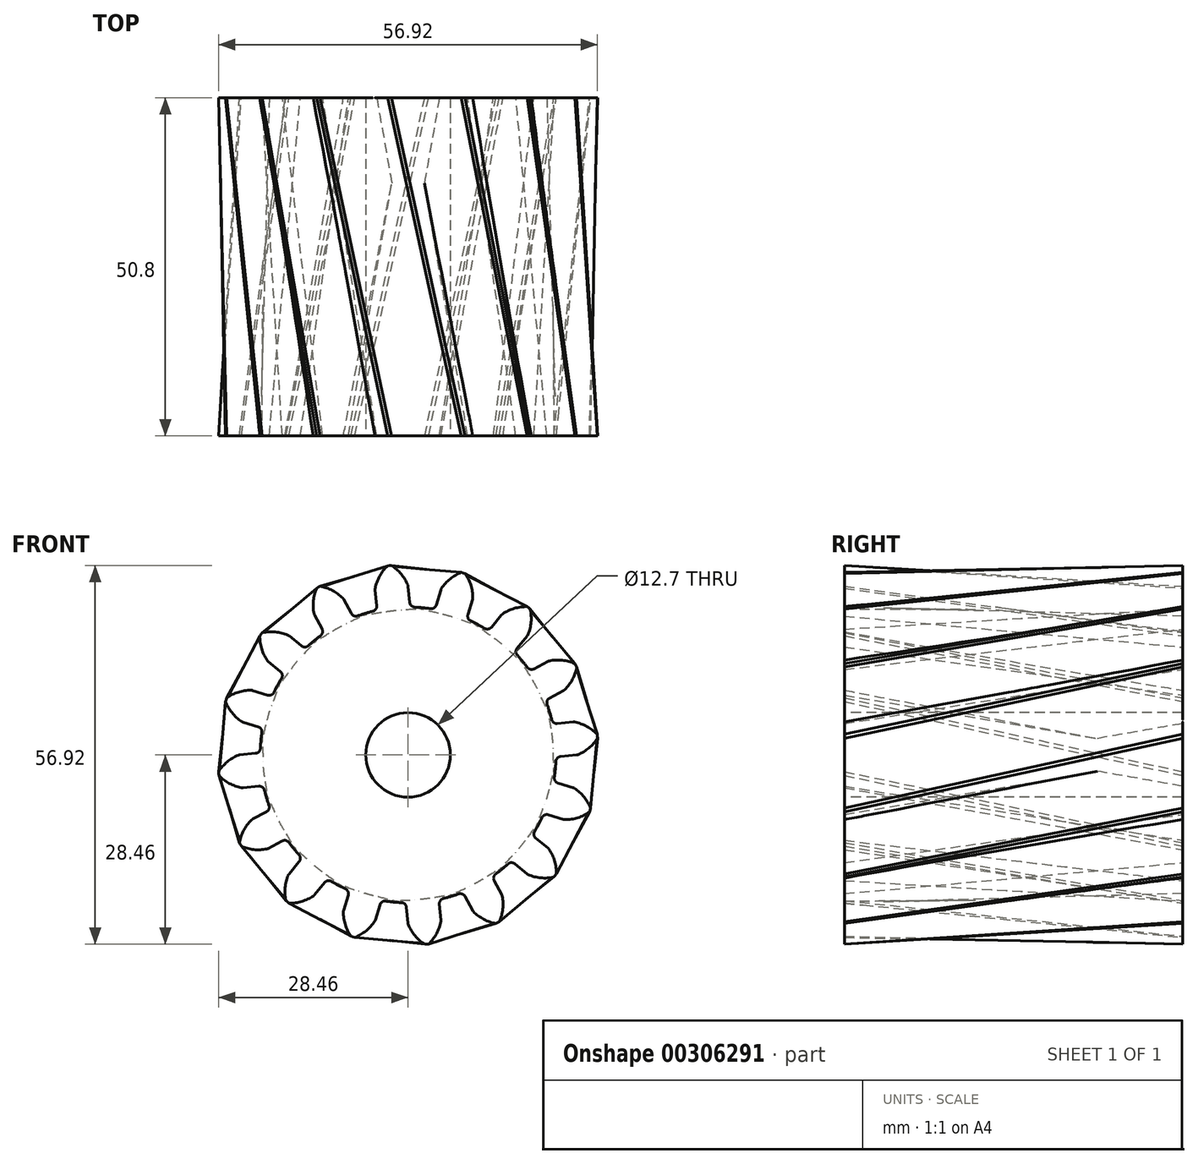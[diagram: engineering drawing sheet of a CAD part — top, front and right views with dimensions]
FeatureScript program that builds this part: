
annotation { "Feature Type Name" : "Feature", "Feature Type Description" : "" }
export const myFeature = defineFeature(function(context is Context, id is Id, definition is map)
    precondition{}
    {
        {
            var Q0;
            Q0=qCreatedBy(makeId("Front.planeOp"),FACE);
            var sketch = newSketch(context, id + "F0", { "sketchPlane" : qUnion([Q0])});
            skArc(sketch, "E0", {"start": v(-5.3, 21.58) * mm, "mid": v(-6.45, 21.27) * mm, "end": v(-7.58, 20.9) * mm});
            skArc(sketch, "E1.trimOffspring", {"start": v(-0.04, 25.51) * mm, "mid": v(-1.05, 27.18) * mm, "end": v(-2.5, 28.46) * mm});
            skLineSegment(sketch, "E2", {"start": v(-2.5, 28.46) * mm, "end": v(-2.8, 28.44) * mm});
            skLineSegment(sketch, "E3", {"start": v(0.01, 25.29) * mm, "end": v(0.25, 22.91) * mm});
            skLineSegment(sketch, "E4.MirrorCS", {"start": v(-3.1, 28.4) * mm, "end": v(-2.8, 28.44) * mm});
            skArc(sketch, "E5.MirrorCS", {"start": v(-4.93, 25.03) * mm, "mid": v(-4.28, 26.86) * mm, "end": v(-3.1, 28.4) * mm});
            skLineSegment(sketch, "E6.MirrorCS", {"start": v(-4.94, 24.8) * mm, "end": v(-4.71, 22.42) * mm});
            skPoint(sketch, "E7.orphan", {"position": v(-4.37, 19) * mm});
            skPoint(sketch, "E8.orphan", {"position": v(0.58, 19.48) * mm});
            skPoint(sketch, "E9.visualSharp", {"position": v(-4.96, 24.91) * mm});
            skArc(sketch, "E9.filletArc", {"start": v(-4.93, 25.03) * mm, "mid": v(-4.95, 24.92) * mm, "end": v(-4.94, 24.8) * mm});
            skPoint(sketch, "E10.visualSharp", {"position": v(0, 25.4) * mm});
            skArc(sketch, "E10.filletArc", {"start": v(0.01, 25.29) * mm, "mid": v(0, 25.4) * mm, "end": v(-0.04, 25.51) * mm});
            skPoint(sketch, "E11.visualSharp", {"position": v(0.31, 22.22) * mm});
            skArc(sketch, "E11.filletArc", {"start": v(0.25, 22.91) * mm, "mid": v(0.49, 22.42) * mm, "end": v(1, 22.2) * mm});
            skPoint(sketch, "E12.visualSharp", {"position": v(-4.64, 21.73) * mm});
            skArc(sketch, "E12.filletArc", {"start": v(-5.3, 21.58) * mm, "mid": v(-4.85, 21.9) * mm, "end": v(-4.71, 22.42) * mm});
            skArc(sketch, "E13.1.0", {"start": v(-14.14, 21.24) * mm, "mid": v(-14.23, 23.18) * mm, "end": v(-13.73, 25.06) * mm});
            skArc(sketch, "E13.1.1", {"start": v(-14.14, 21.24) * mm, "mid": v(-14.1, 21.13) * mm, "end": v(-14.06, 21.02) * mm});
            skLineSegment(sketch, "E13.1.2", {"start": v(-14.06, 21.02) * mm, "end": v(-12.93, 18.91) * mm});
            skArc(sketch, "E13.1.3", {"start": v(-9.67, 23.37) * mm, "mid": v(-9.73, 23.47) * mm, "end": v(-9.8, 23.55) * mm});
            skArc(sketch, "E13.1.4", {"start": v(-9.8, 23.55) * mm, "mid": v(-11.37, 24.7) * mm, "end": v(-13.21, 25.34) * mm});
            skLineSegment(sketch, "E13.1.5", {"start": v(-9.67, 23.37) * mm, "end": v(-8.54, 21.26) * mm});
            skLineSegment(sketch, "E13.1.6", {"start": v(-13.21, 25.34) * mm, "end": v(-13.47, 25.2) * mm});
            skLineSegment(sketch, "E13.1.7", {"start": v(-13.73, 25.06) * mm, "end": v(-13.47, 25.2) * mm});
            skArc(sketch, "E13.1.8", {"start": v(-13.16, 17.9) * mm, "mid": v(-12.86, 18.37) * mm, "end": v(-12.93, 18.91) * mm});
            skArc(sketch, "E13.1.9", {"start": v(-8.54, 21.26) * mm, "mid": v(-8.13, 20.9) * mm, "end": v(-7.58, 20.9) * mm});
            skArc(sketch, "E13.2.0", {"start": v(-21.19, 14.2) * mm, "mid": v(-22.02, 15.97) * mm, "end": v(-22.27, 17.9) * mm});
            skArc(sketch, "E13.2.1", {"start": v(-21.19, 14.2) * mm, "mid": v(-21.12, 14.12) * mm, "end": v(-21.03, 14.04) * mm});
            skLineSegment(sketch, "E13.2.2", {"start": v(-21.03, 14.04) * mm, "end": v(-19.19, 12.53) * mm});
            skArc(sketch, "E13.2.3", {"start": v(-17.87, 17.9) * mm, "mid": v(-17.97, 17.96) * mm, "end": v(-18.07, 18) * mm});
            skArc(sketch, "E13.2.4", {"start": v(-18.07, 18) * mm, "mid": v(-19.96, 18.48) * mm, "end": v(-21.9, 18.35) * mm});
            skLineSegment(sketch, "E13.2.5", {"start": v(-17.87, 17.9) * mm, "end": v(-16.03, 16.37) * mm});
            skLineSegment(sketch, "E13.2.6", {"start": v(-21.9, 18.35) * mm, "end": v(-22.09, 18.13) * mm});
            skLineSegment(sketch, "E13.2.7", {"start": v(-22.27, 17.9) * mm, "end": v(-22.09, 18.13) * mm});
            skArc(sketch, "E13.2.8", {"start": v(-19.01, 11.5) * mm, "mid": v(-18.91, 12.05) * mm, "end": v(-19.19, 12.53) * mm});
            skArc(sketch, "E13.2.9", {"start": v(-16.03, 16.37) * mm, "mid": v(-15.5, 16.2) * mm, "end": v(-15, 16.4) * mm});
            skArc(sketch, "E14.2.3.0", {"start": v(-25.01, 5.02) * mm, "mid": v(-26.45, 6.33) * mm, "end": v(-27.43, 8.01) * mm});
            skArc(sketch, "E14.4.3.0", {"start": v(-25.01, 5.02) * mm, "mid": v(-24.91, 4.96) * mm, "end": v(-24.8, 4.92) * mm});
            skLineSegment(sketch, "E14.8.3.0", {"start": v(-24.8, 4.92) * mm, "end": v(-22.52, 4.23) * mm});
            skArc(sketch, "E14.11.3.0", {"start": v(-23.36, 9.69) * mm, "mid": v(-23.47, 9.71) * mm, "end": v(-23.58, 9.72) * mm});
            skArc(sketch, "E14.15.3.0", {"start": v(-23.58, 9.72) * mm, "mid": v(-25.51, 9.43) * mm, "end": v(-27.26, 8.58) * mm});
            skLineSegment(sketch, "E14.19.3.0", {"start": v(-23.36, 9.69) * mm, "end": v(-21.07, 9) * mm});
            skLineSegment(sketch, "E14.22.3.0", {"start": v(-27.26, 8.58) * mm, "end": v(-27.35, 8.3) * mm});
            skLineSegment(sketch, "E14.25.3.0", {"start": v(-27.43, 8.01) * mm, "end": v(-27.35, 8.3) * mm});
            skArc(sketch, "E14.28.3.0", {"start": v(-21.97, 3.36) * mm, "mid": v(-22.08, 3.9) * mm, "end": v(-22.52, 4.23) * mm});
            skArc(sketch, "E14.32.3.0", {"start": v(-21.07, 9) * mm, "mid": v(-20.53, 9.03) * mm, "end": v(-20.13, 9.41) * mm});
            skArc(sketch, "E14.2.4.0", {"start": v(-25.03, -4.93) * mm, "mid": v(-26.86, -4.28) * mm, "end": v(-28.4, -3.1) * mm});
            skArc(sketch, "E14.4.4.0", {"start": v(-25.03, -4.93) * mm, "mid": v(-24.92, -4.95) * mm, "end": v(-24.8, -4.94) * mm});
            skLineSegment(sketch, "E14.8.4.0", {"start": v(-24.8, -4.94) * mm, "end": v(-22.42, -4.71) * mm});
            skArc(sketch, "E14.11.4.0", {"start": v(-25.29, 0.01) * mm, "mid": v(-25.4, 0) * mm, "end": v(-25.51, -0.04) * mm});
            skArc(sketch, "E14.15.4.0", {"start": v(-25.51, -0.04) * mm, "mid": v(-27.18, -1.05) * mm, "end": v(-28.46, -2.5) * mm});
            skLineSegment(sketch, "E14.19.4.0", {"start": v(-25.29, 0.01) * mm, "end": v(-22.91, 0.25) * mm});
            skLineSegment(sketch, "E14.22.4.0", {"start": v(-28.46, -2.5) * mm, "end": v(-28.44, -2.8) * mm});
            skLineSegment(sketch, "E14.25.4.0", {"start": v(-28.4, -3.1) * mm, "end": v(-28.44, -2.8) * mm});
            skArc(sketch, "E14.28.4.0", {"start": v(-21.58, -5.3) * mm, "mid": v(-21.9, -4.85) * mm, "end": v(-22.42, -4.71) * mm});
            skArc(sketch, "E14.32.4.0", {"start": v(-22.91, 0.25) * mm, "mid": v(-22.42, 0.49) * mm, "end": v(-22.2, 1) * mm});
            skArc(sketch, "E14.2.5.0", {"start": v(-21.24, -14.14) * mm, "mid": v(-23.18, -14.23) * mm, "end": v(-25.06, -13.73) * mm});
            skArc(sketch, "E14.4.5.0", {"start": v(-21.24, -14.14) * mm, "mid": v(-21.13, -14.1) * mm, "end": v(-21.02, -14.06) * mm});
            skLineSegment(sketch, "E14.8.5.0", {"start": v(-21.02, -14.06) * mm, "end": v(-18.91, -12.93) * mm});
            skArc(sketch, "E14.11.5.0", {"start": v(-23.37, -9.67) * mm, "mid": v(-23.47, -9.73) * mm, "end": v(-23.55, -9.8) * mm});
            skArc(sketch, "E14.15.5.0", {"start": v(-23.55, -9.8) * mm, "mid": v(-24.7, -11.37) * mm, "end": v(-25.34, -13.21) * mm});
            skLineSegment(sketch, "E14.19.5.0", {"start": v(-23.37, -9.67) * mm, "end": v(-21.26, -8.54) * mm});
            skLineSegment(sketch, "E14.22.5.0", {"start": v(-25.34, -13.21) * mm, "end": v(-25.2, -13.47) * mm});
            skLineSegment(sketch, "E14.25.5.0", {"start": v(-25.06, -13.73) * mm, "end": v(-25.2, -13.47) * mm});
            skArc(sketch, "E14.28.5.0", {"start": v(-17.9, -13.16) * mm, "mid": v(-18.37, -12.86) * mm, "end": v(-18.91, -12.93) * mm});
            skArc(sketch, "E14.32.5.0", {"start": v(-21.26, -8.54) * mm, "mid": v(-20.9, -8.13) * mm, "end": v(-20.9, -7.58) * mm});
            skArc(sketch, "E14.2.6.0", {"start": v(-14.2, -21.19) * mm, "mid": v(-15.97, -22.02) * mm, "end": v(-17.9, -22.27) * mm});
            skArc(sketch, "E14.4.6.0", {"start": v(-14.2, -21.19) * mm, "mid": v(-14.12, -21.12) * mm, "end": v(-14.04, -21.03) * mm});
            skLineSegment(sketch, "E14.8.6.0", {"start": v(-14.04, -21.03) * mm, "end": v(-12.53, -19.19) * mm});
            skArc(sketch, "E14.11.6.0", {"start": v(-17.9, -17.87) * mm, "mid": v(-17.96, -17.97) * mm, "end": v(-18, -18.07) * mm});
            skArc(sketch, "E14.15.6.0", {"start": v(-18, -18.07) * mm, "mid": v(-18.48, -19.96) * mm, "end": v(-18.35, -21.9) * mm});
            skLineSegment(sketch, "E14.19.6.0", {"start": v(-17.9, -17.87) * mm, "end": v(-16.37, -16.03) * mm});
            skLineSegment(sketch, "E14.22.6.0", {"start": v(-18.35, -21.9) * mm, "end": v(-18.13, -22.09) * mm});
            skLineSegment(sketch, "E14.25.6.0", {"start": v(-17.9, -22.27) * mm, "end": v(-18.13, -22.09) * mm});
            skArc(sketch, "E14.28.6.0", {"start": v(-11.5, -19.01) * mm, "mid": v(-12.05, -18.91) * mm, "end": v(-12.53, -19.19) * mm});
            skArc(sketch, "E14.32.6.0", {"start": v(-16.37, -16.03) * mm, "mid": v(-16.2, -15.5) * mm, "end": v(-16.4, -15) * mm});
            skArc(sketch, "E14.2.7.0", {"start": v(-5.02, -25.01) * mm, "mid": v(-6.33, -26.45) * mm, "end": v(-8.01, -27.43) * mm});
            skArc(sketch, "E14.4.7.0", {"start": v(-5.02, -25.01) * mm, "mid": v(-4.96, -24.91) * mm, "end": v(-4.92, -24.8) * mm});
            skLineSegment(sketch, "E14.8.7.0", {"start": v(-4.92, -24.8) * mm, "end": v(-4.23, -22.52) * mm});
            skArc(sketch, "E14.11.7.0", {"start": v(-9.69, -23.36) * mm, "mid": v(-9.71, -23.47) * mm, "end": v(-9.72, -23.58) * mm});
            skArc(sketch, "E14.15.7.0", {"start": v(-9.72, -23.58) * mm, "mid": v(-9.43, -25.51) * mm, "end": v(-8.58, -27.26) * mm});
            skLineSegment(sketch, "E14.19.7.0", {"start": v(-9.69, -23.36) * mm, "end": v(-9, -21.07) * mm});
            skLineSegment(sketch, "E14.22.7.0", {"start": v(-8.58, -27.26) * mm, "end": v(-8.3, -27.35) * mm});
            skLineSegment(sketch, "E14.25.7.0", {"start": v(-8.01, -27.43) * mm, "end": v(-8.3, -27.35) * mm});
            skArc(sketch, "E14.28.7.0", {"start": v(-3.36, -21.97) * mm, "mid": v(-3.9, -22.08) * mm, "end": v(-4.23, -22.52) * mm});
            skArc(sketch, "E14.32.7.0", {"start": v(-9, -21.07) * mm, "mid": v(-9.03, -20.53) * mm, "end": v(-9.41, -20.13) * mm});
            skArc(sketch, "E14.2.8.0", {"start": v(4.93, -25.03) * mm, "mid": v(4.28, -26.86) * mm, "end": v(3.1, -28.4) * mm});
            skArc(sketch, "E14.4.8.0", {"start": v(4.93, -25.03) * mm, "mid": v(4.95, -24.92) * mm, "end": v(4.94, -24.8) * mm});
            skLineSegment(sketch, "E14.8.8.0", {"start": v(4.94, -24.8) * mm, "end": v(4.71, -22.42) * mm});
            skArc(sketch, "E14.11.8.0", {"start": v(-0.01, -25.29) * mm, "mid": v(0, -25.4) * mm, "end": v(0.04, -25.51) * mm});
            skArc(sketch, "E14.15.8.0", {"start": v(0.04, -25.51) * mm, "mid": v(1.05, -27.18) * mm, "end": v(2.5, -28.46) * mm});
            skLineSegment(sketch, "E14.19.8.0", {"start": v(-0.01, -25.29) * mm, "end": v(-0.25, -22.91) * mm});
            skLineSegment(sketch, "E14.22.8.0", {"start": v(2.5, -28.46) * mm, "end": v(2.8, -28.44) * mm});
            skLineSegment(sketch, "E14.25.8.0", {"start": v(3.1, -28.4) * mm, "end": v(2.8, -28.44) * mm});
            skArc(sketch, "E14.28.8.0", {"start": v(5.3, -21.58) * mm, "mid": v(4.85, -21.9) * mm, "end": v(4.71, -22.42) * mm});
            skArc(sketch, "E14.32.8.0", {"start": v(-0.25, -22.91) * mm, "mid": v(-0.49, -22.42) * mm, "end": v(-1, -22.2) * mm});
            skArc(sketch, "E14.2.9.0", {"start": v(14.14, -21.24) * mm, "mid": v(14.23, -23.18) * mm, "end": v(13.73, -25.06) * mm});
            skArc(sketch, "E14.4.9.0", {"start": v(14.14, -21.24) * mm, "mid": v(14.1, -21.13) * mm, "end": v(14.06, -21.02) * mm});
            skLineSegment(sketch, "E14.8.9.0", {"start": v(14.06, -21.02) * mm, "end": v(12.93, -18.91) * mm});
            skArc(sketch, "E14.11.9.0", {"start": v(9.67, -23.37) * mm, "mid": v(9.73, -23.47) * mm, "end": v(9.8, -23.55) * mm});
            skArc(sketch, "E14.15.9.0", {"start": v(9.8, -23.55) * mm, "mid": v(11.37, -24.7) * mm, "end": v(13.21, -25.34) * mm});
            skLineSegment(sketch, "E14.19.9.0", {"start": v(9.67, -23.37) * mm, "end": v(8.54, -21.26) * mm});
            skLineSegment(sketch, "E14.22.9.0", {"start": v(13.21, -25.34) * mm, "end": v(13.47, -25.2) * mm});
            skLineSegment(sketch, "E14.25.9.0", {"start": v(13.73, -25.06) * mm, "end": v(13.47, -25.2) * mm});
            skArc(sketch, "E14.28.9.0", {"start": v(13.16, -17.9) * mm, "mid": v(12.86, -18.37) * mm, "end": v(12.93, -18.91) * mm});
            skArc(sketch, "E14.32.9.0", {"start": v(8.54, -21.26) * mm, "mid": v(8.13, -20.9) * mm, "end": v(7.58, -20.9) * mm});
            skArc(sketch, "E14.2.10.0", {"start": v(21.19, -14.2) * mm, "mid": v(22.02, -15.97) * mm, "end": v(22.27, -17.9) * mm});
            skArc(sketch, "E14.4.10.0", {"start": v(21.19, -14.2) * mm, "mid": v(21.12, -14.12) * mm, "end": v(21.03, -14.04) * mm});
            skLineSegment(sketch, "E14.8.10.0", {"start": v(21.03, -14.04) * mm, "end": v(19.19, -12.53) * mm});
            skArc(sketch, "E14.11.10.0", {"start": v(17.87, -17.9) * mm, "mid": v(17.97, -17.96) * mm, "end": v(18.07, -18) * mm});
            skArc(sketch, "E14.15.10.0", {"start": v(18.07, -18) * mm, "mid": v(19.96, -18.48) * mm, "end": v(21.9, -18.35) * mm});
            skLineSegment(sketch, "E14.19.10.0", {"start": v(17.87, -17.9) * mm, "end": v(16.03, -16.37) * mm});
            skLineSegment(sketch, "E14.22.10.0", {"start": v(21.9, -18.35) * mm, "end": v(22.09, -18.13) * mm});
            skLineSegment(sketch, "E14.25.10.0", {"start": v(22.27, -17.9) * mm, "end": v(22.09, -18.13) * mm});
            skArc(sketch, "E14.28.10.0", {"start": v(19.01, -11.5) * mm, "mid": v(18.91, -12.05) * mm, "end": v(19.19, -12.53) * mm});
            skArc(sketch, "E14.32.10.0", {"start": v(16.03, -16.37) * mm, "mid": v(15.5, -16.2) * mm, "end": v(15, -16.4) * mm});
            skArc(sketch, "E14.2.11.0", {"start": v(25.01, -5.02) * mm, "mid": v(26.45, -6.33) * mm, "end": v(27.43, -8.01) * mm});
            skArc(sketch, "E14.4.11.0", {"start": v(25.01, -5.02) * mm, "mid": v(24.91, -4.96) * mm, "end": v(24.8, -4.92) * mm});
            skLineSegment(sketch, "E14.8.11.0", {"start": v(24.8, -4.92) * mm, "end": v(22.52, -4.23) * mm});
            skArc(sketch, "E14.11.11.0", {"start": v(23.36, -9.69) * mm, "mid": v(23.47, -9.71) * mm, "end": v(23.58, -9.72) * mm});
            skArc(sketch, "E14.15.11.0", {"start": v(23.58, -9.72) * mm, "mid": v(25.51, -9.43) * mm, "end": v(27.26, -8.58) * mm});
            skLineSegment(sketch, "E14.19.11.0", {"start": v(23.36, -9.69) * mm, "end": v(21.07, -9) * mm});
            skLineSegment(sketch, "E14.22.11.0", {"start": v(27.26, -8.58) * mm, "end": v(27.35, -8.3) * mm});
            skLineSegment(sketch, "E14.25.11.0", {"start": v(27.43, -8.01) * mm, "end": v(27.35, -8.3) * mm});
            skArc(sketch, "E14.28.11.0", {"start": v(21.97, -3.36) * mm, "mid": v(22.08, -3.9) * mm, "end": v(22.52, -4.23) * mm});
            skArc(sketch, "E14.32.11.0", {"start": v(21.07, -9) * mm, "mid": v(20.53, -9.03) * mm, "end": v(20.13, -9.41) * mm});
            skArc(sketch, "E14.2.12.0", {"start": v(25.03, 4.93) * mm, "mid": v(26.86, 4.28) * mm, "end": v(28.4, 3.1) * mm});
            skArc(sketch, "E14.4.12.0", {"start": v(25.03, 4.93) * mm, "mid": v(24.92, 4.95) * mm, "end": v(24.8, 4.94) * mm});
            skLineSegment(sketch, "E14.8.12.0", {"start": v(24.8, 4.94) * mm, "end": v(22.42, 4.71) * mm});
            skArc(sketch, "E14.11.12.0", {"start": v(25.29, -0.01) * mm, "mid": v(25.4, 0) * mm, "end": v(25.51, 0.04) * mm});
            skArc(sketch, "E14.15.12.0", {"start": v(25.51, 0.04) * mm, "mid": v(27.18, 1.05) * mm, "end": v(28.46, 2.5) * mm});
            skLineSegment(sketch, "E14.19.12.0", {"start": v(25.29, -0.01) * mm, "end": v(22.91, -0.25) * mm});
            skLineSegment(sketch, "E14.22.12.0", {"start": v(28.46, 2.5) * mm, "end": v(28.44, 2.8) * mm});
            skLineSegment(sketch, "E14.25.12.0", {"start": v(28.4, 3.1) * mm, "end": v(28.44, 2.8) * mm});
            skArc(sketch, "E14.28.12.0", {"start": v(21.58, 5.3) * mm, "mid": v(21.9, 4.85) * mm, "end": v(22.42, 4.71) * mm});
            skArc(sketch, "E14.32.12.0", {"start": v(22.91, -0.25) * mm, "mid": v(22.42, -0.49) * mm, "end": v(22.2, -1) * mm});
            skArc(sketch, "E14.2.13.0", {"start": v(21.24, 14.14) * mm, "mid": v(23.18, 14.23) * mm, "end": v(25.06, 13.73) * mm});
            skArc(sketch, "E14.4.13.0", {"start": v(21.24, 14.14) * mm, "mid": v(21.13, 14.1) * mm, "end": v(21.02, 14.06) * mm});
            skLineSegment(sketch, "E14.8.13.0", {"start": v(21.02, 14.06) * mm, "end": v(18.91, 12.93) * mm});
            skArc(sketch, "E14.11.13.0", {"start": v(23.37, 9.67) * mm, "mid": v(23.47, 9.73) * mm, "end": v(23.55, 9.8) * mm});
            skArc(sketch, "E14.15.13.0", {"start": v(23.55, 9.8) * mm, "mid": v(24.7, 11.37) * mm, "end": v(25.34, 13.21) * mm});
            skLineSegment(sketch, "E14.19.13.0", {"start": v(23.37, 9.67) * mm, "end": v(21.26, 8.54) * mm});
            skLineSegment(sketch, "E14.22.13.0", {"start": v(25.34, 13.21) * mm, "end": v(25.2, 13.47) * mm});
            skLineSegment(sketch, "E14.25.13.0", {"start": v(25.06, 13.73) * mm, "end": v(25.2, 13.47) * mm});
            skArc(sketch, "E14.28.13.0", {"start": v(17.9, 13.16) * mm, "mid": v(18.37, 12.86) * mm, "end": v(18.91, 12.93) * mm});
            skArc(sketch, "E14.32.13.0", {"start": v(21.26, 8.54) * mm, "mid": v(20.9, 8.13) * mm, "end": v(20.9, 7.58) * mm});
            skArc(sketch, "E14.2.14.0", {"start": v(14.2, 21.19) * mm, "mid": v(15.97, 22.02) * mm, "end": v(17.9, 22.27) * mm});
            skArc(sketch, "E14.4.14.0", {"start": v(14.2, 21.19) * mm, "mid": v(14.12, 21.12) * mm, "end": v(14.04, 21.03) * mm});
            skLineSegment(sketch, "E14.8.14.0", {"start": v(14.04, 21.03) * mm, "end": v(12.53, 19.19) * mm});
            skArc(sketch, "E14.11.14.0", {"start": v(17.9, 17.87) * mm, "mid": v(17.96, 17.97) * mm, "end": v(18, 18.07) * mm});
            skArc(sketch, "E14.15.14.0", {"start": v(18, 18.07) * mm, "mid": v(18.48, 19.96) * mm, "end": v(18.35, 21.9) * mm});
            skLineSegment(sketch, "E14.19.14.0", {"start": v(17.9, 17.87) * mm, "end": v(16.37, 16.03) * mm});
            skLineSegment(sketch, "E14.22.14.0", {"start": v(18.35, 21.9) * mm, "end": v(18.13, 22.09) * mm});
            skLineSegment(sketch, "E14.25.14.0", {"start": v(17.9, 22.27) * mm, "end": v(18.13, 22.09) * mm});
            skArc(sketch, "E14.28.14.0", {"start": v(11.5, 19.01) * mm, "mid": v(12.05, 18.91) * mm, "end": v(12.53, 19.19) * mm});
            skArc(sketch, "E14.32.14.0", {"start": v(16.37, 16.03) * mm, "mid": v(16.2, 15.5) * mm, "end": v(16.4, 15) * mm});
            skArc(sketch, "E14.2.15.0", {"start": v(5.02, 25.01) * mm, "mid": v(6.33, 26.45) * mm, "end": v(8.01, 27.43) * mm});
            skArc(sketch, "E14.4.15.0", {"start": v(5.02, 25.01) * mm, "mid": v(4.96, 24.91) * mm, "end": v(4.92, 24.8) * mm});
            skLineSegment(sketch, "E14.8.15.0", {"start": v(4.92, 24.8) * mm, "end": v(4.23, 22.52) * mm});
            skArc(sketch, "E14.11.15.0", {"start": v(9.69, 23.36) * mm, "mid": v(9.71, 23.47) * mm, "end": v(9.72, 23.58) * mm});
            skArc(sketch, "E14.15.15.0", {"start": v(9.72, 23.58) * mm, "mid": v(9.43, 25.51) * mm, "end": v(8.58, 27.26) * mm});
            skLineSegment(sketch, "E14.19.15.0", {"start": v(9.69, 23.36) * mm, "end": v(9, 21.07) * mm});
            skLineSegment(sketch, "E14.22.15.0", {"start": v(8.58, 27.26) * mm, "end": v(8.3, 27.35) * mm});
            skLineSegment(sketch, "E14.25.15.0", {"start": v(8.01, 27.43) * mm, "end": v(8.3, 27.35) * mm});
            skArc(sketch, "E14.28.15.0", {"start": v(3.36, 21.97) * mm, "mid": v(3.9, 22.08) * mm, "end": v(4.23, 22.52) * mm});
            skArc(sketch, "E14.32.15.0", {"start": v(9, 21.07) * mm, "mid": v(9.03, 20.53) * mm, "end": v(9.41, 20.13) * mm});
            skArc(sketch, "E15.trimOffspring", {"start": v(-13.16, 17.9) * mm, "mid": v(-14.1, 17.18) * mm, "end": v(-15, 16.4) * mm});
            skArc(sketch, "E16.trimOffspring", {"start": v(-19.01, 11.5) * mm, "mid": v(-19.6, 10.48) * mm, "end": v(-20.13, 9.41) * mm});
            skArc(sketch, "E17.trimOffspring", {"start": v(-21.97, 3.36) * mm, "mid": v(-22.12, 2.18) * mm, "end": v(-22.2, 1) * mm});
            skArc(sketch, "E18.trimOffspring", {"start": v(-21.58, -5.3) * mm, "mid": v(-21.27, -6.45) * mm, "end": v(-20.9, -7.58) * mm});
            skArc(sketch, "E19.trimOffspring", {"start": v(-17.9, -13.16) * mm, "mid": v(-17.18, -14.1) * mm, "end": v(-16.4, -15) * mm});
            skArc(sketch, "E20.trimOffspring", {"start": v(-11.5, -19.01) * mm, "mid": v(-10.48, -19.6) * mm, "end": v(-9.41, -20.13) * mm});
            skArc(sketch, "E21.trimOffspring", {"start": v(-3.36, -21.97) * mm, "mid": v(-2.18, -22.12) * mm, "end": v(-1, -22.2) * mm});
            skArc(sketch, "E22.trimOffspring", {"start": v(5.3, -21.58) * mm, "mid": v(6.45, -21.27) * mm, "end": v(7.58, -20.9) * mm});
            skArc(sketch, "E23.trimOffspring", {"start": v(13.16, -17.9) * mm, "mid": v(14.1, -17.18) * mm, "end": v(15, -16.4) * mm});
            skArc(sketch, "E24.trimOffspring", {"start": v(19.01, -11.5) * mm, "mid": v(19.6, -10.48) * mm, "end": v(20.13, -9.41) * mm});
            skArc(sketch, "E25.trimOffspring", {"start": v(21.97, -3.36) * mm, "mid": v(22.12, -2.18) * mm, "end": v(22.2, -1) * mm});
            skArc(sketch, "E26.trimOffspring", {"start": v(21.58, 5.3) * mm, "mid": v(21.27, 6.45) * mm, "end": v(20.9, 7.58) * mm});
            skArc(sketch, "E27.trimOffspring", {"start": v(17.9, 13.16) * mm, "mid": v(17.18, 14.1) * mm, "end": v(16.4, 15) * mm});
            skArc(sketch, "E28.trimOffspring", {"start": v(11.5, 19.01) * mm, "mid": v(10.48, 19.6) * mm, "end": v(9.41, 20.13) * mm});
            skArc(sketch, "E29.trimOffspring", {"start": v(3.36, 21.97) * mm, "mid": v(2.18, 22.12) * mm, "end": v(1, 22.2) * mm});
            skSolve(sketch);
        }
        {
            var Q0;
            Q0=makeQuery(id+"F0.imprint","IMPRINT",FACE,{"disambiguationData":[TD([[makeQuery(id+"F0.imprint","IMPRINT",EDGE,{"derivedFrom":sQuery(id+"F0.wireOp",EDGE,"E0")}),1.0]])]});
            cPlane(context, id + "F1", {"entities" : qUnion([Q0]), "cplaneType" : CPlaneType.OFFSET, "offset" : 50.8 * mm, "width" : 152.4 * mm, "height" : 152.4 * mm});
        }
        {
            var Q0;
            Q0=qCreatedBy(id+"F1.planeOp",FACE);
            var sketch = newSketch(context, id + "F2", { "sketchPlane" : qUnion([Q0])});
            skLineSegment(sketch, "E30.0.0", {"start": v(8.54, -21.26) * mm, "end": v(9.67, -23.37) * mm});
            skArc(sketch, "E30.0.1", {"start": v(9.67, -23.37) * mm, "mid": v(9.73, -23.47) * mm, "end": v(9.8, -23.55) * mm});
            skArc(sketch, "E30.0.2", {"start": v(9.8, -23.55) * mm, "mid": v(11.37, -24.7) * mm, "end": v(13.21, -25.34) * mm});
            skLineSegment(sketch, "E30.0.3", {"start": v(13.21, -25.34) * mm, "end": v(13.47, -25.2) * mm});
            skLineSegment(sketch, "E30.0.4", {"start": v(13.47, -25.2) * mm, "end": v(13.73, -25.06) * mm});
            skArc(sketch, "E30.0.5", {"start": v(13.73, -25.06) * mm, "mid": v(14.23, -23.18) * mm, "end": v(14.14, -21.24) * mm});
            skArc(sketch, "E30.0.6", {"start": v(14.14, -21.24) * mm, "mid": v(14.1, -21.13) * mm, "end": v(14.06, -21.02) * mm});
            skLineSegment(sketch, "E30.0.7", {"start": v(14.06, -21.02) * mm, "end": v(12.93, -18.91) * mm});
            skArc(sketch, "E30.0.8", {"start": v(12.93, -18.91) * mm, "mid": v(12.86, -18.37) * mm, "end": v(13.16, -17.9) * mm});
            skArc(sketch, "E30.0.9", {"start": v(13.16, -17.9) * mm, "mid": v(14.1, -17.18) * mm, "end": v(15, -16.4) * mm});
            skArc(sketch, "E30.0.10", {"start": v(15, -16.4) * mm, "mid": v(15.5, -16.2) * mm, "end": v(16.03, -16.37) * mm});
            skLineSegment(sketch, "E30.0.11", {"start": v(16.03, -16.37) * mm, "end": v(17.87, -17.9) * mm});
            skArc(sketch, "E30.0.12", {"start": v(17.87, -17.9) * mm, "mid": v(17.97, -17.96) * mm, "end": v(18.07, -18) * mm});
            skArc(sketch, "E30.0.13", {"start": v(18.07, -18) * mm, "mid": v(19.96, -18.48) * mm, "end": v(21.9, -18.35) * mm});
            skLineSegment(sketch, "E30.0.14", {"start": v(21.9, -18.35) * mm, "end": v(22.09, -18.13) * mm});
            skLineSegment(sketch, "E30.0.15", {"start": v(22.09, -18.13) * mm, "end": v(22.27, -17.9) * mm});
            skArc(sketch, "E30.0.16", {"start": v(22.27, -17.9) * mm, "mid": v(22.02, -15.97) * mm, "end": v(21.19, -14.2) * mm});
            skArc(sketch, "E30.0.17", {"start": v(21.19, -14.2) * mm, "mid": v(21.12, -14.12) * mm, "end": v(21.03, -14.04) * mm});
            skLineSegment(sketch, "E30.0.18", {"start": v(21.03, -14.04) * mm, "end": v(19.19, -12.53) * mm});
            skArc(sketch, "E30.0.19", {"start": v(19.19, -12.53) * mm, "mid": v(18.91, -12.05) * mm, "end": v(19.01, -11.5) * mm});
            skArc(sketch, "E30.0.20", {"start": v(19.01, -11.5) * mm, "mid": v(19.6, -10.48) * mm, "end": v(20.13, -9.41) * mm});
            skArc(sketch, "E30.0.21", {"start": v(20.13, -9.41) * mm, "mid": v(20.53, -9.03) * mm, "end": v(21.07, -9) * mm});
            skLineSegment(sketch, "E30.0.22", {"start": v(21.07, -9) * mm, "end": v(23.36, -9.69) * mm});
            skArc(sketch, "E30.0.23", {"start": v(23.36, -9.69) * mm, "mid": v(23.47, -9.71) * mm, "end": v(23.58, -9.72) * mm});
            skArc(sketch, "E30.0.24", {"start": v(23.58, -9.72) * mm, "mid": v(25.51, -9.43) * mm, "end": v(27.26, -8.58) * mm});
            skLineSegment(sketch, "E30.0.25", {"start": v(27.26, -8.58) * mm, "end": v(27.35, -8.3) * mm});
            skLineSegment(sketch, "E30.0.26", {"start": v(27.35, -8.3) * mm, "end": v(27.43, -8.01) * mm});
            skArc(sketch, "E30.0.27", {"start": v(27.43, -8.01) * mm, "mid": v(26.45, -6.33) * mm, "end": v(25.01, -5.02) * mm});
            skArc(sketch, "E30.0.28", {"start": v(25.01, -5.02) * mm, "mid": v(24.91, -4.96) * mm, "end": v(24.8, -4.92) * mm});
            skLineSegment(sketch, "E30.0.29", {"start": v(24.8, -4.92) * mm, "end": v(22.52, -4.23) * mm});
            skArc(sketch, "E30.0.30", {"start": v(22.52, -4.23) * mm, "mid": v(22.08, -3.9) * mm, "end": v(21.97, -3.36) * mm});
            skArc(sketch, "E30.0.31", {"start": v(21.97, -3.36) * mm, "mid": v(22.12, -2.18) * mm, "end": v(22.2, -1) * mm});
            skArc(sketch, "E30.0.32", {"start": v(22.2, -1) * mm, "mid": v(22.42, -0.49) * mm, "end": v(22.91, -0.25) * mm});
            skLineSegment(sketch, "E30.0.33", {"start": v(22.91, -0.25) * mm, "end": v(25.29, -0.01) * mm});
            skArc(sketch, "E30.0.34", {"start": v(25.29, -0.01) * mm, "mid": v(25.4, 0) * mm, "end": v(25.51, 0.04) * mm});
            skArc(sketch, "E30.0.35", {"start": v(25.51, 0.04) * mm, "mid": v(27.18, 1.05) * mm, "end": v(28.46, 2.5) * mm});
            skLineSegment(sketch, "E30.0.36", {"start": v(28.46, 2.5) * mm, "end": v(28.44, 2.8) * mm});
            skLineSegment(sketch, "E30.0.37", {"start": v(28.44, 2.8) * mm, "end": v(28.4, 3.1) * mm});
            skArc(sketch, "E30.0.38", {"start": v(28.4, 3.1) * mm, "mid": v(26.86, 4.28) * mm, "end": v(25.03, 4.93) * mm});
            skArc(sketch, "E30.0.39", {"start": v(25.03, 4.93) * mm, "mid": v(24.92, 4.95) * mm, "end": v(24.8, 4.94) * mm});
            skLineSegment(sketch, "E30.0.40", {"start": v(24.8, 4.94) * mm, "end": v(22.42, 4.71) * mm});
            skArc(sketch, "E30.0.41", {"start": v(22.42, 4.71) * mm, "mid": v(21.9, 4.85) * mm, "end": v(21.58, 5.3) * mm});
            skArc(sketch, "E30.0.42", {"start": v(21.58, 5.3) * mm, "mid": v(21.27, 6.45) * mm, "end": v(20.9, 7.58) * mm});
            skArc(sketch, "E30.0.43", {"start": v(20.9, 7.58) * mm, "mid": v(20.9, 8.13) * mm, "end": v(21.26, 8.54) * mm});
            skLineSegment(sketch, "E30.0.44", {"start": v(21.26, 8.54) * mm, "end": v(23.37, 9.67) * mm});
            skArc(sketch, "E30.0.45", {"start": v(23.37, 9.67) * mm, "mid": v(23.47, 9.73) * mm, "end": v(23.55, 9.8) * mm});
            skArc(sketch, "E30.0.46", {"start": v(23.55, 9.8) * mm, "mid": v(24.7, 11.37) * mm, "end": v(25.34, 13.21) * mm});
            skLineSegment(sketch, "E30.0.47", {"start": v(25.34, 13.21) * mm, "end": v(25.2, 13.47) * mm});
            skLineSegment(sketch, "E30.0.48", {"start": v(25.2, 13.47) * mm, "end": v(25.06, 13.73) * mm});
            skArc(sketch, "E30.0.49", {"start": v(25.06, 13.73) * mm, "mid": v(23.18, 14.23) * mm, "end": v(21.24, 14.14) * mm});
            skArc(sketch, "E30.0.50", {"start": v(21.24, 14.14) * mm, "mid": v(21.13, 14.1) * mm, "end": v(21.02, 14.06) * mm});
            skLineSegment(sketch, "E30.0.51", {"start": v(21.02, 14.06) * mm, "end": v(18.91, 12.93) * mm});
            skArc(sketch, "E30.0.52", {"start": v(18.91, 12.93) * mm, "mid": v(18.37, 12.86) * mm, "end": v(17.9, 13.16) * mm});
            skArc(sketch, "E30.0.53", {"start": v(17.9, 13.16) * mm, "mid": v(17.18, 14.1) * mm, "end": v(16.4, 15) * mm});
            skArc(sketch, "E30.0.54", {"start": v(16.4, 15) * mm, "mid": v(16.2, 15.5) * mm, "end": v(16.37, 16.03) * mm});
            skLineSegment(sketch, "E30.0.55", {"start": v(16.37, 16.03) * mm, "end": v(17.9, 17.87) * mm});
            skArc(sketch, "E30.0.56", {"start": v(17.9, 17.87) * mm, "mid": v(17.96, 17.97) * mm, "end": v(18, 18.07) * mm});
            skArc(sketch, "E30.0.57", {"start": v(18, 18.07) * mm, "mid": v(18.48, 19.96) * mm, "end": v(18.35, 21.9) * mm});
            skLineSegment(sketch, "E30.0.58", {"start": v(18.35, 21.9) * mm, "end": v(18.13, 22.09) * mm});
            skLineSegment(sketch, "E30.0.59", {"start": v(18.13, 22.09) * mm, "end": v(17.9, 22.27) * mm});
            skArc(sketch, "E30.0.60", {"start": v(17.9, 22.27) * mm, "mid": v(15.97, 22.02) * mm, "end": v(14.2, 21.19) * mm});
            skArc(sketch, "E30.0.61", {"start": v(14.2, 21.19) * mm, "mid": v(14.12, 21.12) * mm, "end": v(14.04, 21.03) * mm});
            skLineSegment(sketch, "E30.0.62", {"start": v(14.04, 21.03) * mm, "end": v(12.53, 19.19) * mm});
            skArc(sketch, "E30.0.63", {"start": v(12.53, 19.19) * mm, "mid": v(12.05, 18.91) * mm, "end": v(11.5, 19.01) * mm});
            skArc(sketch, "E30.0.64", {"start": v(11.5, 19.01) * mm, "mid": v(10.48, 19.6) * mm, "end": v(9.41, 20.13) * mm});
            skArc(sketch, "E30.0.65", {"start": v(9.41, 20.13) * mm, "mid": v(9.03, 20.53) * mm, "end": v(9, 21.07) * mm});
            skLineSegment(sketch, "E30.0.66", {"start": v(9, 21.07) * mm, "end": v(9.69, 23.36) * mm});
            skArc(sketch, "E30.0.67", {"start": v(9.69, 23.36) * mm, "mid": v(9.71, 23.47) * mm, "end": v(9.72, 23.58) * mm});
            skArc(sketch, "E30.0.68", {"start": v(9.72, 23.58) * mm, "mid": v(9.43, 25.51) * mm, "end": v(8.58, 27.26) * mm});
            skLineSegment(sketch, "E30.0.69", {"start": v(8.58, 27.26) * mm, "end": v(8.3, 27.35) * mm});
            skLineSegment(sketch, "E30.0.70", {"start": v(8.3, 27.35) * mm, "end": v(8.01, 27.43) * mm});
            skArc(sketch, "E30.0.71", {"start": v(8.01, 27.43) * mm, "mid": v(6.33, 26.45) * mm, "end": v(5.02, 25.01) * mm});
            skArc(sketch, "E30.0.72", {"start": v(5.02, 25.01) * mm, "mid": v(4.96, 24.91) * mm, "end": v(4.92, 24.8) * mm});
            skLineSegment(sketch, "E30.0.73", {"start": v(4.92, 24.8) * mm, "end": v(4.23, 22.52) * mm});
            skArc(sketch, "E30.0.74", {"start": v(4.23, 22.52) * mm, "mid": v(3.9, 22.08) * mm, "end": v(3.36, 21.97) * mm});
            skArc(sketch, "E30.0.75", {"start": v(3.36, 21.97) * mm, "mid": v(2.18, 22.12) * mm, "end": v(1, 22.2) * mm});
            skArc(sketch, "E30.0.76", {"start": v(1, 22.2) * mm, "mid": v(0.49, 22.42) * mm, "end": v(0.25, 22.91) * mm});
            skLineSegment(sketch, "E30.0.77", {"start": v(0.25, 22.91) * mm, "end": v(0.01, 25.29) * mm});
            skArc(sketch, "E30.0.78", {"start": v(0.01, 25.29) * mm, "mid": v(0, 25.4) * mm, "end": v(-0.04, 25.51) * mm});
            skArc(sketch, "E30.0.79", {"start": v(-0.04, 25.51) * mm, "mid": v(-1.05, 27.18) * mm, "end": v(-2.5, 28.46) * mm});
            skLineSegment(sketch, "E30.0.80", {"start": v(-2.5, 28.46) * mm, "end": v(-2.8, 28.44) * mm});
            skLineSegment(sketch, "E30.0.81", {"start": v(-2.8, 28.44) * mm, "end": v(-3.1, 28.4) * mm});
            skArc(sketch, "E30.0.82", {"start": v(-3.1, 28.4) * mm, "mid": v(-4.28, 26.86) * mm, "end": v(-4.93, 25.03) * mm});
            skArc(sketch, "E30.0.83", {"start": v(-4.93, 25.03) * mm, "mid": v(-4.95, 24.92) * mm, "end": v(-4.94, 24.8) * mm});
            skLineSegment(sketch, "E30.0.84", {"start": v(-4.94, 24.8) * mm, "end": v(-4.71, 22.42) * mm});
            skArc(sketch, "E30.0.85", {"start": v(-4.71, 22.42) * mm, "mid": v(-4.85, 21.9) * mm, "end": v(-5.3, 21.58) * mm});
            skArc(sketch, "E30.0.86", {"start": v(-5.3, 21.58) * mm, "mid": v(-6.45, 21.27) * mm, "end": v(-7.58, 20.9) * mm});
            skArc(sketch, "E30.0.87", {"start": v(-7.58, 20.9) * mm, "mid": v(-8.13, 20.9) * mm, "end": v(-8.54, 21.26) * mm});
            skLineSegment(sketch, "E30.0.88", {"start": v(-8.54, 21.26) * mm, "end": v(-9.67, 23.37) * mm});
            skArc(sketch, "E30.0.89", {"start": v(-9.67, 23.37) * mm, "mid": v(-9.73, 23.47) * mm, "end": v(-9.8, 23.55) * mm});
            skArc(sketch, "E30.0.90", {"start": v(-9.8, 23.55) * mm, "mid": v(-11.37, 24.7) * mm, "end": v(-13.21, 25.34) * mm});
            skLineSegment(sketch, "E30.0.91", {"start": v(-13.21, 25.34) * mm, "end": v(-13.47, 25.2) * mm});
            skLineSegment(sketch, "E30.0.92", {"start": v(-13.47, 25.2) * mm, "end": v(-13.73, 25.06) * mm});
            skArc(sketch, "E30.0.93", {"start": v(-13.73, 25.06) * mm, "mid": v(-14.23, 23.18) * mm, "end": v(-14.14, 21.24) * mm});
            skArc(sketch, "E30.0.94", {"start": v(-14.14, 21.24) * mm, "mid": v(-14.1, 21.13) * mm, "end": v(-14.06, 21.02) * mm});
            skLineSegment(sketch, "E30.0.95", {"start": v(-14.06, 21.02) * mm, "end": v(-12.93, 18.91) * mm});
            skArc(sketch, "E30.0.96", {"start": v(-12.93, 18.91) * mm, "mid": v(-12.86, 18.37) * mm, "end": v(-13.16, 17.9) * mm});
            skArc(sketch, "E30.0.97", {"start": v(-13.16, 17.9) * mm, "mid": v(-14.1, 17.18) * mm, "end": v(-15, 16.4) * mm});
            skArc(sketch, "E30.0.98", {"start": v(-15, 16.4) * mm, "mid": v(-15.5, 16.2) * mm, "end": v(-16.03, 16.37) * mm});
            skLineSegment(sketch, "E30.0.99", {"start": v(-16.03, 16.37) * mm, "end": v(-17.87, 17.9) * mm});
            skArc(sketch, "E30.0.100", {"start": v(-17.87, 17.9) * mm, "mid": v(-17.97, 17.96) * mm, "end": v(-18.07, 18) * mm});
            skArc(sketch, "E30.0.101", {"start": v(-18.07, 18) * mm, "mid": v(-19.96, 18.48) * mm, "end": v(-21.9, 18.35) * mm});
            skLineSegment(sketch, "E30.0.102", {"start": v(-21.9, 18.35) * mm, "end": v(-22.09, 18.13) * mm});
            skLineSegment(sketch, "E30.0.103", {"start": v(-22.09, 18.13) * mm, "end": v(-22.27, 17.9) * mm});
            skArc(sketch, "E30.0.104", {"start": v(-22.27, 17.9) * mm, "mid": v(-22.02, 15.97) * mm, "end": v(-21.19, 14.2) * mm});
            skArc(sketch, "E30.0.105", {"start": v(-21.19, 14.2) * mm, "mid": v(-21.12, 14.12) * mm, "end": v(-21.03, 14.04) * mm});
            skLineSegment(sketch, "E30.0.106", {"start": v(-21.03, 14.04) * mm, "end": v(-19.19, 12.53) * mm});
            skArc(sketch, "E30.0.107", {"start": v(-19.19, 12.53) * mm, "mid": v(-18.91, 12.05) * mm, "end": v(-19.01, 11.5) * mm});
            skArc(sketch, "E30.0.108", {"start": v(-19.01, 11.5) * mm, "mid": v(-19.6, 10.48) * mm, "end": v(-20.13, 9.41) * mm});
            skArc(sketch, "E30.0.109", {"start": v(-20.13, 9.41) * mm, "mid": v(-20.53, 9.03) * mm, "end": v(-21.07, 9) * mm});
            skLineSegment(sketch, "E30.0.110", {"start": v(-21.07, 9) * mm, "end": v(-23.36, 9.69) * mm});
            skArc(sketch, "E30.0.111", {"start": v(-23.36, 9.69) * mm, "mid": v(-23.47, 9.71) * mm, "end": v(-23.58, 9.72) * mm});
            skArc(sketch, "E30.0.112", {"start": v(-23.58, 9.72) * mm, "mid": v(-25.51, 9.43) * mm, "end": v(-27.26, 8.58) * mm});
            skLineSegment(sketch, "E30.0.113", {"start": v(-27.26, 8.58) * mm, "end": v(-27.35, 8.3) * mm});
            skLineSegment(sketch, "E30.0.114", {"start": v(-27.35, 8.3) * mm, "end": v(-27.43, 8.01) * mm});
            skArc(sketch, "E30.0.115", {"start": v(-27.43, 8.01) * mm, "mid": v(-26.45, 6.33) * mm, "end": v(-25.01, 5.02) * mm});
            skArc(sketch, "E30.0.116", {"start": v(-25.01, 5.02) * mm, "mid": v(-24.91, 4.96) * mm, "end": v(-24.8, 4.92) * mm});
            skLineSegment(sketch, "E30.0.117", {"start": v(-24.8, 4.92) * mm, "end": v(-22.52, 4.23) * mm});
            skArc(sketch, "E30.0.118", {"start": v(-22.52, 4.23) * mm, "mid": v(-22.08, 3.9) * mm, "end": v(-21.97, 3.36) * mm});
            skArc(sketch, "E30.0.119", {"start": v(-21.97, 3.36) * mm, "mid": v(-22.12, 2.18) * mm, "end": v(-22.2, 1) * mm});
            skArc(sketch, "E30.0.120", {"start": v(-22.2, 1) * mm, "mid": v(-22.42, 0.49) * mm, "end": v(-22.91, 0.25) * mm});
            skLineSegment(sketch, "E30.0.121", {"start": v(-22.91, 0.25) * mm, "end": v(-25.29, 0.01) * mm});
            skArc(sketch, "E30.0.122", {"start": v(-25.29, 0.01) * mm, "mid": v(-25.4, 0) * mm, "end": v(-25.51, -0.04) * mm});
            skArc(sketch, "E30.0.123", {"start": v(-25.51, -0.04) * mm, "mid": v(-27.18, -1.05) * mm, "end": v(-28.46, -2.5) * mm});
            skLineSegment(sketch, "E30.0.124", {"start": v(-28.46, -2.5) * mm, "end": v(-28.44, -2.8) * mm});
            skLineSegment(sketch, "E30.0.125", {"start": v(-28.44, -2.8) * mm, "end": v(-28.4, -3.1) * mm});
            skArc(sketch, "E30.0.126", {"start": v(-28.4, -3.1) * mm, "mid": v(-26.86, -4.28) * mm, "end": v(-25.03, -4.93) * mm});
            skArc(sketch, "E30.0.127", {"start": v(-25.03, -4.93) * mm, "mid": v(-24.92, -4.95) * mm, "end": v(-24.8, -4.94) * mm});
            skLineSegment(sketch, "E30.0.128", {"start": v(-24.8, -4.94) * mm, "end": v(-22.42, -4.71) * mm});
            skArc(sketch, "E30.0.129", {"start": v(-22.42, -4.71) * mm, "mid": v(-21.9, -4.85) * mm, "end": v(-21.58, -5.3) * mm});
            skArc(sketch, "E30.0.130", {"start": v(-21.58, -5.3) * mm, "mid": v(-21.27, -6.45) * mm, "end": v(-20.9, -7.58) * mm});
            skArc(sketch, "E30.0.131", {"start": v(-20.9, -7.58) * mm, "mid": v(-20.9, -8.13) * mm, "end": v(-21.26, -8.54) * mm});
            skLineSegment(sketch, "E30.0.132", {"start": v(-21.26, -8.54) * mm, "end": v(-23.37, -9.67) * mm});
            skArc(sketch, "E30.0.133", {"start": v(-23.37, -9.67) * mm, "mid": v(-23.47, -9.73) * mm, "end": v(-23.55, -9.8) * mm});
            skArc(sketch, "E30.0.134", {"start": v(-23.55, -9.8) * mm, "mid": v(-24.7, -11.37) * mm, "end": v(-25.34, -13.21) * mm});
            skLineSegment(sketch, "E30.0.135", {"start": v(-25.34, -13.21) * mm, "end": v(-25.2, -13.47) * mm});
            skLineSegment(sketch, "E30.0.136", {"start": v(-25.2, -13.47) * mm, "end": v(-25.06, -13.73) * mm});
            skArc(sketch, "E30.0.137", {"start": v(-25.06, -13.73) * mm, "mid": v(-23.18, -14.23) * mm, "end": v(-21.24, -14.14) * mm});
            skArc(sketch, "E30.0.138", {"start": v(-21.24, -14.14) * mm, "mid": v(-21.13, -14.1) * mm, "end": v(-21.02, -14.06) * mm});
            skLineSegment(sketch, "E30.0.139", {"start": v(-21.02, -14.06) * mm, "end": v(-18.91, -12.93) * mm});
            skArc(sketch, "E30.0.140", {"start": v(-18.91, -12.93) * mm, "mid": v(-18.37, -12.86) * mm, "end": v(-17.9, -13.16) * mm});
            skArc(sketch, "E30.0.141", {"start": v(-17.9, -13.16) * mm, "mid": v(-17.18, -14.1) * mm, "end": v(-16.4, -15) * mm});
            skArc(sketch, "E30.0.142", {"start": v(-16.4, -15) * mm, "mid": v(-16.2, -15.5) * mm, "end": v(-16.37, -16.03) * mm});
            skLineSegment(sketch, "E30.0.143", {"start": v(-16.37, -16.03) * mm, "end": v(-17.9, -17.87) * mm});
            skArc(sketch, "E30.0.144", {"start": v(-17.9, -17.87) * mm, "mid": v(-17.96, -17.97) * mm, "end": v(-18, -18.07) * mm});
            skArc(sketch, "E30.0.145", {"start": v(-18, -18.07) * mm, "mid": v(-18.48, -19.96) * mm, "end": v(-18.35, -21.9) * mm});
            skLineSegment(sketch, "E30.0.146", {"start": v(-18.35, -21.9) * mm, "end": v(-18.13, -22.09) * mm});
            skLineSegment(sketch, "E30.0.147", {"start": v(-18.13, -22.09) * mm, "end": v(-17.9, -22.27) * mm});
            skArc(sketch, "E30.0.148", {"start": v(-17.9, -22.27) * mm, "mid": v(-15.97, -22.02) * mm, "end": v(-14.2, -21.19) * mm});
            skArc(sketch, "E30.0.149", {"start": v(-14.2, -21.19) * mm, "mid": v(-14.12, -21.12) * mm, "end": v(-14.04, -21.03) * mm});
            skLineSegment(sketch, "E30.0.150", {"start": v(-14.04, -21.03) * mm, "end": v(-12.53, -19.19) * mm});
            skArc(sketch, "E30.0.151", {"start": v(-12.53, -19.19) * mm, "mid": v(-12.05, -18.91) * mm, "end": v(-11.5, -19.01) * mm});
            skArc(sketch, "E30.0.152", {"start": v(-11.5, -19.01) * mm, "mid": v(-10.48, -19.6) * mm, "end": v(-9.41, -20.13) * mm});
            skArc(sketch, "E30.0.153", {"start": v(-9.41, -20.13) * mm, "mid": v(-9.03, -20.53) * mm, "end": v(-9, -21.07) * mm});
            skLineSegment(sketch, "E30.0.154", {"start": v(-9, -21.07) * mm, "end": v(-9.69, -23.36) * mm});
            skArc(sketch, "E30.0.155", {"start": v(-9.69, -23.36) * mm, "mid": v(-9.71, -23.47) * mm, "end": v(-9.72, -23.58) * mm});
            skArc(sketch, "E30.0.156", {"start": v(-9.72, -23.58) * mm, "mid": v(-9.43, -25.51) * mm, "end": v(-8.58, -27.26) * mm});
            skLineSegment(sketch, "E30.0.157", {"start": v(-8.58, -27.26) * mm, "end": v(-8.3, -27.35) * mm});
            skLineSegment(sketch, "E30.0.158", {"start": v(-8.3, -27.35) * mm, "end": v(-8.01, -27.43) * mm});
            skArc(sketch, "E30.0.159", {"start": v(-8.01, -27.43) * mm, "mid": v(-6.33, -26.45) * mm, "end": v(-5.02, -25.01) * mm});
            skArc(sketch, "E30.0.160", {"start": v(-5.02, -25.01) * mm, "mid": v(-4.96, -24.91) * mm, "end": v(-4.92, -24.8) * mm});
            skLineSegment(sketch, "E30.0.161", {"start": v(-4.92, -24.8) * mm, "end": v(-4.23, -22.52) * mm});
            skArc(sketch, "E30.0.162", {"start": v(-4.23, -22.52) * mm, "mid": v(-3.9, -22.08) * mm, "end": v(-3.36, -21.97) * mm});
            skArc(sketch, "E30.0.163", {"start": v(-3.36, -21.97) * mm, "mid": v(-2.18, -22.12) * mm, "end": v(-1, -22.2) * mm});
            skArc(sketch, "E30.0.164", {"start": v(-1, -22.2) * mm, "mid": v(-0.49, -22.42) * mm, "end": v(-0.25, -22.91) * mm});
            skLineSegment(sketch, "E30.0.165", {"start": v(-0.25, -22.91) * mm, "end": v(-0.01, -25.29) * mm});
            skArc(sketch, "E30.0.166", {"start": v(-0.01, -25.29) * mm, "mid": v(0, -25.4) * mm, "end": v(0.04, -25.51) * mm});
            skArc(sketch, "E30.0.167", {"start": v(0.04, -25.51) * mm, "mid": v(1.05, -27.18) * mm, "end": v(2.5, -28.46) * mm});
            skLineSegment(sketch, "E30.0.168", {"start": v(2.5, -28.46) * mm, "end": v(2.8, -28.44) * mm});
            skLineSegment(sketch, "E30.0.169", {"start": v(2.8, -28.44) * mm, "end": v(3.1, -28.4) * mm});
            skArc(sketch, "E30.0.170", {"start": v(3.1, -28.4) * mm, "mid": v(4.28, -26.86) * mm, "end": v(4.93, -25.03) * mm});
            skArc(sketch, "E30.0.171", {"start": v(4.93, -25.03) * mm, "mid": v(4.95, -24.92) * mm, "end": v(4.94, -24.8) * mm});
            skLineSegment(sketch, "E30.0.172", {"start": v(4.94, -24.8) * mm, "end": v(4.71, -22.42) * mm});
            skArc(sketch, "E30.0.173", {"start": v(4.71, -22.42) * mm, "mid": v(4.85, -21.9) * mm, "end": v(5.3, -21.58) * mm});
            skArc(sketch, "E30.0.174", {"start": v(5.3, -21.58) * mm, "mid": v(6.45, -21.27) * mm, "end": v(7.58, -20.9) * mm});
            skArc(sketch, "E30.0.175", {"start": v(7.58, -20.9) * mm, "mid": v(8.13, -20.9) * mm, "end": v(8.54, -21.26) * mm});
            skSolve(sketch);
        }
        {
            var Q0;
            Q0=makeQuery(id+"F2.imprint","IMPRINT",FACE,{"disambiguationData":[TD([[makeQuery(id+"F2.imprint","IMPRINT",EDGE,{"derivedFrom":sQuery(id+"F2.wireOp",EDGE,"E30.0.0")}),1.0]])]});
            var Q1;
            Q1=makeQuery(id+"F0.imprint","IMPRINT",FACE,{"disambiguationData":[TD([[makeQuery(id+"F0.imprint","IMPRINT",EDGE,{"derivedFrom":sQuery(id+"F0.wireOp",EDGE,"E0")}),1.0]])]});
            var Q2;
            Q2=sQuery(id+"F2.wireOp",VERTEX,"E30.0.78.start");
            var Q3;
            Q3=sQuery(id+"F0.wireOp",VERTEX,"E13.1.3.start");
            loft(context, id + "F3", {"sheetProfilesArray" : [{ "sheetProfileEntities" : qUnion([Q0]) }, { "sheetProfileEntities" : qUnion([Q1]) }], "matchConnections" : true, "connections" : [{ "connectionEntities" : qUnion([Q2, Q3]), "connectionEdgeQueries" : qUnion([]), "connectionEdgeParameters" : [] }]});
        }
        {
            var Q0;
            Q0=makeQuery(id+"F3.opLoft","CAP_FACE",FACE,{"disambiguationData":[OSD([makeQuery(id+"F2.imprint","IMPRINT",FACE,{"disambiguationData":[TD([[makeQuery(id+"F2.imprint","IMPRINT",EDGE,{"derivedFrom":sQuery(id+"F2.wireOp",EDGE,"E30.0.0")}),1.0]])]})])],"isStart":true});
            var sketch = newSketch(context, id + "F4", { "sketchPlane" : qUnion([Q0])});
            skCircle(sketch, "E31", {"center": v(0, 0) * mm, "radius": 6.35 * mm});
            skSolve(sketch);
        }
        {
            var Q0;
            Q0 = qSketchRegion(id + "F4", true);
            extrude(context, id + "F5", {"entities" : qUnion([Q0]), "operationType" : NewBodyOperationType.REMOVE, "oppositeDirection" : true, "depth" : 50.8 * mm});
        }
    });
